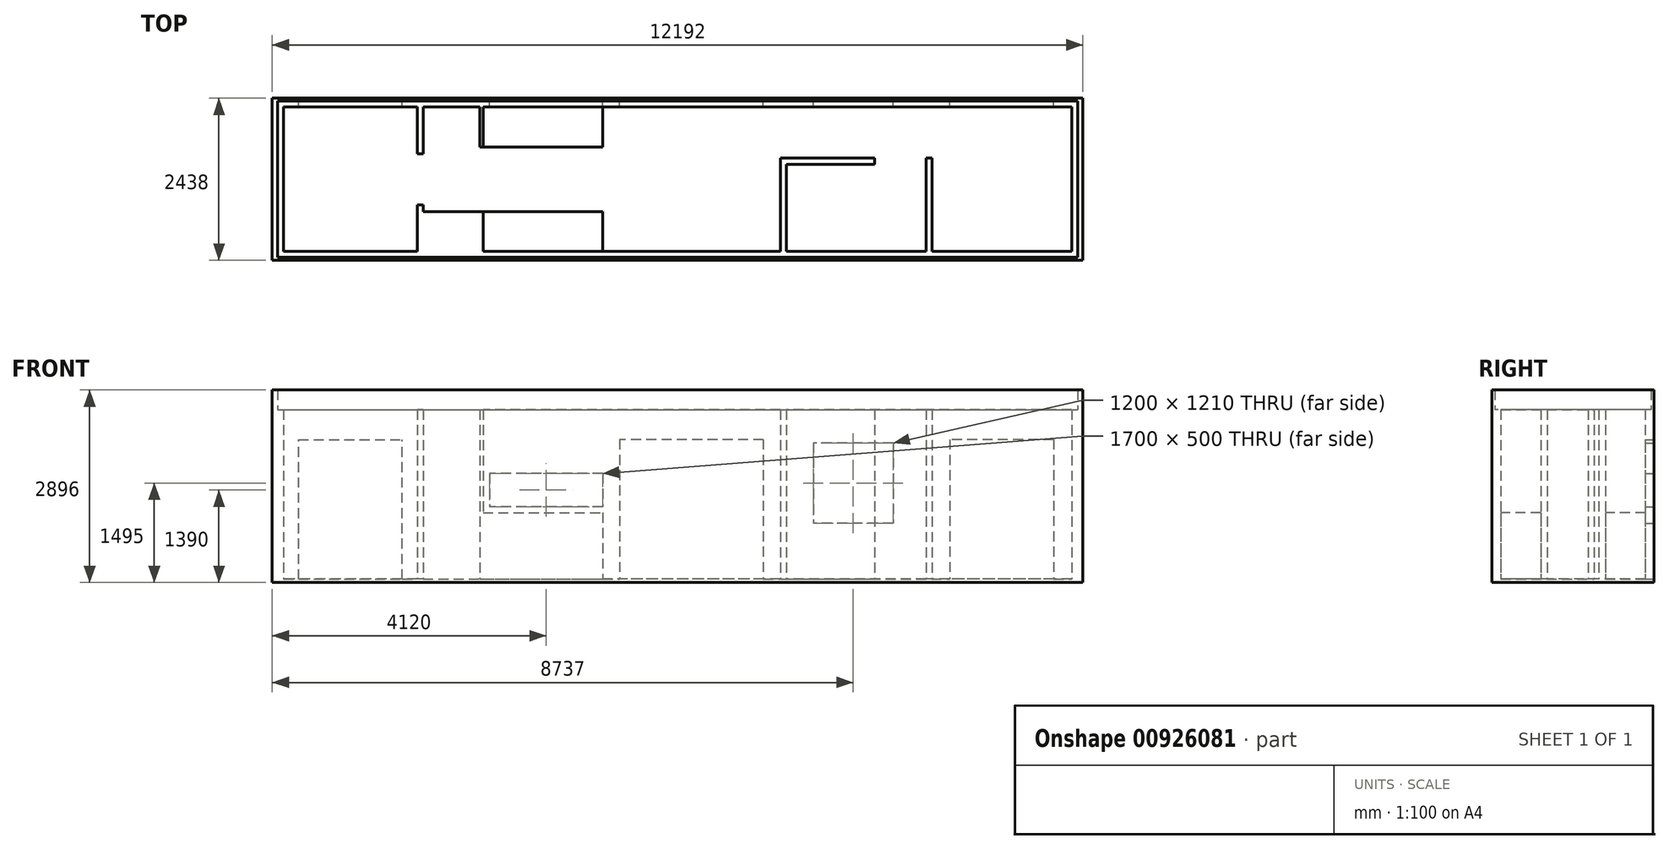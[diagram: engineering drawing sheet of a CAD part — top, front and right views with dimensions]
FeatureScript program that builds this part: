
annotation { "Feature Type Name" : "Feature", "Feature Type Description" : "" }
export const myFeature = defineFeature(function(context is Context, id is Id, definition is map)
    precondition{}
    {
        {
            var Q0;
            Q0=qCreatedBy(makeId("Top.planeOp"),FACE);
            var sketch = newSketch(context, id + "F0", { "sketchPlane" : qUnion([Q0])});
            skLineSegment(sketch, "E0.bottom", {"start": v(-6016, 1176) * mm, "end": v(6016, 1176) * mm});
            skLineSegment(sketch, "E0.top", {"start": v(-6016, -1176) * mm, "end": v(6016, -1176) * mm});
            skLineSegment(sketch, "E0.left", {"start": v(-6016, 1176) * mm, "end": v(-6016, -1176) * mm});
            skLineSegment(sketch, "E0.right", {"start": v(6016, 1176) * mm, "end": v(6016, -1176) * mm});
            skPoint(sketch, "E0.middle", {"position": v(0, 0) * mm});
            skLineSegment(sketch, "E1.bottom", {"start": v(-6096, 1219) * mm, "end": v(6096, 1219) * mm});
            skLineSegment(sketch, "E1.top", {"start": v(-6096, -1219) * mm, "end": v(6096, -1219) * mm});
            skLineSegment(sketch, "E1.left", {"start": v(-6096, 1219) * mm, "end": v(-6096, -1219) * mm});
            skLineSegment(sketch, "E1.right", {"start": v(6096, 1219) * mm, "end": v(6096, -1219) * mm});
            skSolve(sketch);
        }
        {
            var Q0;
            Q0=makeQuery(id+"F0.imprint","IMPRINT",FACE,{"disambiguationData":[TD([[makeQuery(id+"F0.imprint","IMPRINT",EDGE,{"derivedFrom":sQuery(id+"F0.wireOp",EDGE,"E0.bottom")}),1.0]])]});
            extrude(context, id + "F1", {"entities" : qUnion([Q0]), "depth" : 2896 * mm, "offsetDistance" : 25 * mm});
        }
        {
            var Q0;
            Q0=makeQuery(id+"F0.imprint","IMPRINT",FACE,{"disambiguationData":[TD([[makeQuery(id+"F0.imprint","IMPRINT",EDGE,{"derivedFrom":sQuery(id+"F0.wireOp",EDGE,"E0.bottom")}),-1.0]])]});
            extrude(context, id + "F2", {"entities" : qUnion([Q0]), "operationType" : NewBodyOperationType.ADD, "depth" : 50 * mm, "offsetDistance" : 25 * mm});
        }
        {
            var Q0;
            Q0=makeQuery(id+"F2.opExtrude","CAP_FACE",FACE,{"disambiguationData":[OSD([sQuery(id+"F0.wireOp",EDGE,"E0.bottom"),sQuery(id+"F0.wireOp",EDGE,"E0.top"),sQuery(id+"F0.wireOp",EDGE,"E0.left"),sQuery(id+"F0.wireOp",EDGE,"E0.right")])],"isStart":false});
            var sketch = newSketch(context, id + "F3", { "sketchPlane" : qUnion([Q0])});
            skLineSegment(sketch, "E2.bottom", {"start": v(-6016, 1176) * mm, "end": v(-5926, 1176) * mm});
            skLineSegment(sketch, "E2.top", {"start": v(-6016, -1176) * mm, "end": v(-5926, -1176) * mm});
            skLineSegment(sketch, "E2.left", {"start": v(-6016, 1176) * mm, "end": v(-6016, -1176) * mm});
            skLineSegment(sketch, "E2.right", {"start": v(-5926, 1086) * mm, "end": v(-5926, -1086) * mm});
            skLineSegment(sketch, "E3.bottom", {"start": v(-5926, 1176) * mm, "end": v(6016, 1176) * mm});
            skLineSegment(sketch, "E3.top", {"start": v(-5926, 1086) * mm, "end": v(5926, 1086) * mm});
            skLineSegment(sketch, "E4.top", {"start": v(5926, -1176) * mm, "end": v(6016, -1176) * mm});
            skLineSegment(sketch, "E4.left", {"start": v(5926, 1086) * mm, "end": v(5926, -1086) * mm});
            skLineSegment(sketch, "E5.bottom", {"start": v(5926, -1086) * mm, "end": v(-5926, -1086) * mm});
            skLineSegment(sketch, "E5.top", {"start": v(5926, -1176) * mm, "end": v(-5926, -1176) * mm});
            skSolve(sketch);
        }
        {
            var Q0;
            Q0=makeQuery(id+"F3.imprint","IMPRINT",FACE,{"disambiguationData":[TD([[makeQuery(id+"F3.imprint","IMPRINT",EDGE,{"derivedFrom":sQuery(id+"F3.wireOp",EDGE,"E2.bottom")}),-1.0]])]});
            extrude(context, id + "F4", {"entities" : qUnion([Q0]), "operationType" : NewBodyOperationType.ADD, "depth" : 2550 * mm, "offsetDistance" : 25 * mm});
        }
        {
            var Q0;
            Q0=makeQuery(id+"F2.opExtrude","CAP_FACE",FACE,{"disambiguationData":[OSD([sQuery(id+"F0.wireOp",EDGE,"E0.bottom"),sQuery(id+"F0.wireOp",EDGE,"E0.top"),sQuery(id+"F0.wireOp",EDGE,"E0.left"),sQuery(id+"F0.wireOp",EDGE,"E0.right")])],"isStart":false});
            var sketch = newSketch(context, id + "F5", { "sketchPlane" : qUnion([Q0])});
            skLineSegment(sketch, "E6.bottom", {"start": v(-3826, 1086) * mm, "end": v(-3916, 1086) * mm});
            skLineSegment(sketch, "E6.top", {"start": v(-3826, 385) * mm, "end": v(-3916, 385) * mm});
            skLineSegment(sketch, "E6.left", {"start": v(-3826, 1086) * mm, "end": v(-3826, 385) * mm});
            skLineSegment(sketch, "E6.right", {"start": v(-3916, 1086) * mm, "end": v(-3916, 385) * mm});
            skLineSegment(sketch, "E7.bottom", {"start": v(-3826, -385) * mm, "end": v(-3916, -385) * mm});
            skLineSegment(sketch, "E7.top", {"start": v(-3826, -1086) * mm, "end": v(-3916, -1086) * mm});
            skLineSegment(sketch, "E7.left", {"start": v(-3826, -385) * mm, "end": v(-3826, -1086) * mm});
            skLineSegment(sketch, "E7.right", {"start": v(-3916, -385) * mm, "end": v(-3916, -1086) * mm});
            skLineSegment(sketch, "E8.bottom", {"start": v(-3826, -1086) * mm, "end": v(-2926, -1086) * mm});
            skLineSegment(sketch, "E8.top", {"start": v(-3826, -486) * mm, "end": v(-2926, -486) * mm});
            skLineSegment(sketch, "E8.left", {"start": v(-3826, -1086) * mm, "end": v(-3826, -486) * mm});
            skLineSegment(sketch, "E8.right", {"start": v(-2926, -1086) * mm, "end": v(-2926, -486) * mm});
            skLineSegment(sketch, "E9.bottom", {"start": v(-2926, -486) * mm, "end": v(-1126, -486) * mm});
            skLineSegment(sketch, "E9.top", {"start": v(-2926, -1086) * mm, "end": v(-1126, -1086) * mm});
            skLineSegment(sketch, "E9.left", {"start": v(-2926, -486) * mm, "end": v(-2926, -1086) * mm});
            skLineSegment(sketch, "E9.right", {"start": v(-1126, -486) * mm, "end": v(-1126, -1086) * mm});
            skLineSegment(sketch, "E10.bottom", {"start": v(3826, -1086) * mm, "end": v(3736, -1086) * mm});
            skLineSegment(sketch, "E10.top", {"start": v(3826, 316) * mm, "end": v(3736, 316) * mm});
            skLineSegment(sketch, "E10.left", {"start": v(3826, -1086) * mm, "end": v(3826, 316) * mm});
            skLineSegment(sketch, "E10.right", {"start": v(3736, -1086) * mm, "end": v(3736, 316) * mm});
            skLineSegment(sketch, "E11.bottom", {"start": v(1546, -1086) * mm, "end": v(1636, -1086) * mm});
            skLineSegment(sketch, "E11.top", {"start": v(1546, 316) * mm, "end": v(1636, 316) * mm});
            skLineSegment(sketch, "E11.left", {"start": v(1546, -1086) * mm, "end": v(1546, 316) * mm});
            skLineSegment(sketch, "E11.right", {"start": v(1636, -1086) * mm, "end": v(1636, 226) * mm});
            skLineSegment(sketch, "E12.bottom", {"start": v(1636, 316) * mm, "end": v(2966, 316) * mm});
            skLineSegment(sketch, "E12.top", {"start": v(1636, 226) * mm, "end": v(2966, 226) * mm});
            skLineSegment(sketch, "E12.right", {"start": v(2966, 316) * mm, "end": v(2966, 226) * mm});
            skLineSegment(sketch, "E13.bottom", {"start": v(-2976, 1086) * mm, "end": v(-2926, 1086) * mm});
            skLineSegment(sketch, "E13.top", {"start": v(-2976, 486) * mm, "end": v(-2926, 486) * mm});
            skLineSegment(sketch, "E13.left", {"start": v(-2976, 1086) * mm, "end": v(-2976, 486) * mm});
            skLineSegment(sketch, "E13.right", {"start": v(-2926, 1086) * mm, "end": v(-2926, 486) * mm});
            skLineSegment(sketch, "E14.bottom", {"start": v(-2926, 486) * mm, "end": v(-1126, 486) * mm});
            skLineSegment(sketch, "E14.top", {"start": v(-2926, 1086) * mm, "end": v(-1126, 1086) * mm});
            skLineSegment(sketch, "E14.left", {"start": v(-2926, 486) * mm, "end": v(-2926, 1086) * mm});
            skLineSegment(sketch, "E14.right", {"start": v(-1126, 486) * mm, "end": v(-1126, 1086) * mm});
            skSolve(sketch);
        }
        {
            var Q0;
            Q0=makeQuery(id+"F5.imprint","IMPRINT",FACE,{"disambiguationData":[TD([[makeQuery(id+"F5.imprint","IMPRINT",EDGE,{"derivedFrom":sQuery(id+"F5.wireOp",EDGE,"E6.bottom")}),-1.0]])]});
            var Q1;
            {var subQ1=sQuery(id+"F5.wireOp",EDGE,"E7.bottom");Q1=makeQuery(id+"F5.imprint","IMPRINT",FACE,{"disambiguationData":[TD([[makeQuery(id+"F5.imprint","IMPRINT",EDGE,{"derivedFrom":subQ1}),1.0]])]});}
            var Q2;
            Q2=makeQuery(id+"F5.imprint","IMPRINT",FACE,{"disambiguationData":[TD([[makeQuery(id+"F5.imprint","IMPRINT",EDGE,{"derivedFrom":sQuery(id+"F5.wireOp",EDGE,"E11.bottom")}),-1.0]])]});
            var Q3;
            Q3=makeQuery(id+"F5.imprint","IMPRINT",FACE,{"disambiguationData":[TD([[makeQuery(id+"F5.imprint","IMPRINT",EDGE,{"derivedFrom":sQuery(id+"F5.wireOp",EDGE,"E10.bottom")}),-1.0]])]});
            var Q4;
            Q4=makeQuery(id+"F5.imprint","IMPRINT",FACE,{"disambiguationData":[TD([[makeQuery(id+"F5.imprint","IMPRINT",EDGE,{"derivedFrom":sQuery(id+"F5.wireOp",EDGE,"E13.bottom")}),-1.0]])]});
            extrude(context, id + "F6", {"entities" : qUnion([Q0, Q1, Q2, Q3, Q4]), "operationType" : NewBodyOperationType.ADD, "depth" : 2550 * mm, "offsetDistance" : 25 * mm});
        }
        {
            var Q0;
            Q0=makeQuery(id+"F5.imprint","IMPRINT",FACE,{"disambiguationData":[TD([[makeQuery(id+"F5.imprint","IMPRINT",EDGE,{"derivedFrom":sQuery(id+"F5.wireOp",EDGE,"E8.right")}),-1.0]])]});
            var Q1;
            Q1=makeQuery(id+"F5.imprint","IMPRINT",FACE,{"disambiguationData":[TD([[makeQuery(id+"F5.imprint","IMPRINT",EDGE,{"derivedFrom":sQuery(id+"F5.wireOp",EDGE,"E13.right")}),1.0]])]});
            extrude(context, id + "F7", {"entities" : qUnion([Q0, Q1]), "operationType" : NewBodyOperationType.ADD, "depth" : 1000 * mm, "offsetDistance" : 25 * mm});
        }
        {
            var Q0;
            {var subQ0=sQuery(id+"F5.wireOp",EDGE,"E8.bottom");Q0=makeQuery(id+"F5.imprint","IMPRINT",FACE,{"disambiguationData":[TD([[makeQuery(id+"F5.imprint","IMPRINT",EDGE,{"derivedFrom":subQ0}),-1.0]])]});}
            extrude(context, id + "F8", {"entities" : qUnion([Q0]), "operationType" : NewBodyOperationType.ADD, "depth" : 2550 * mm, "offsetDistance" : 25 * mm});
        }
        {
            var Q0;
            Q0=makeQuery(id+"F1.opExtrude","SWEPT_FACE",FACE,{"disambiguationData":[OSD([sQuery(id+"F0.wireOp",EDGE,"E1.bottom")])]});
            var sketch = newSketch(context, id + "F9", { "sketchPlane" : qUnion([Q0])});
            skLineSegment(sketch, "E15.bottom", {"start": v(-1290, 2150) * mm, "end": v(870, 2150) * mm});
            skLineSegment(sketch, "E15.top", {"start": v(-1290, 50) * mm, "end": v(870, 50) * mm});
            skLineSegment(sketch, "E15.left", {"start": v(-1290, 2150) * mm, "end": v(-1290, 50) * mm});
            skLineSegment(sketch, "E15.right", {"start": v(870, 2150) * mm, "end": v(870, 50) * mm});
            skLineSegment(sketch, "E16.bottom", {"start": v(1126, 1640) * mm, "end": v(2826, 1640) * mm});
            skLineSegment(sketch, "E16.top", {"start": v(1126, 1140) * mm, "end": v(2826, 1140) * mm});
            skLineSegment(sketch, "E16.left", {"start": v(1126, 1640) * mm, "end": v(1126, 1140) * mm});
            skLineSegment(sketch, "E16.right", {"start": v(2826, 1640) * mm, "end": v(2826, 1140) * mm});
            skLineSegment(sketch, "E17.bottom", {"start": v(-5656, 2150) * mm, "end": v(-4096, 2150) * mm});
            skLineSegment(sketch, "E17.top", {"start": v(-5656, 50) * mm, "end": v(-4096, 50) * mm});
            skLineSegment(sketch, "E17.left", {"start": v(-5656, 2150) * mm, "end": v(-5656, 50) * mm});
            skLineSegment(sketch, "E17.right", {"start": v(-4096, 2150) * mm, "end": v(-4096, 50) * mm});
            skLineSegment(sketch, "E18.bottom", {"start": v(5701, 50) * mm, "end": v(4141, 50) * mm});
            skLineSegment(sketch, "E18.top", {"start": v(5701, 2150) * mm, "end": v(4141, 2150) * mm});
            skLineSegment(sketch, "E18.left", {"start": v(5701, 50) * mm, "end": v(5701, 2150) * mm});
            skLineSegment(sketch, "E18.right", {"start": v(4141, 50) * mm, "end": v(4141, 2150) * mm});
            skLineSegment(sketch, "E19.bottom", {"start": v(-3241, 2100) * mm, "end": v(-2041, 2100) * mm});
            skLineSegment(sketch, "E19.top", {"start": v(-3241, 890) * mm, "end": v(-2041, 890) * mm});
            skLineSegment(sketch, "E19.left", {"start": v(-3241, 2100) * mm, "end": v(-3241, 890) * mm});
            skLineSegment(sketch, "E19.right", {"start": v(-2041, 2100) * mm, "end": v(-2041, 890) * mm});
            skSolve(sketch);
        }
        {
            var Q0;
            Q0=makeQuery(id+"F9.imprint","IMPRINT",FACE,{"disambiguationData":[TD([[makeQuery(id+"F9.imprint","IMPRINT",EDGE,{"derivedFrom":sQuery(id+"F9.wireOp",EDGE,"E15.bottom")}),-1.0]])]});
            var Q1;
            Q1=makeQuery(id+"F9.imprint","IMPRINT",FACE,{"disambiguationData":[TD([[makeQuery(id+"F9.imprint","IMPRINT",EDGE,{"derivedFrom":sQuery(id+"F9.wireOp",EDGE,"E16.bottom")}),-1.0]])]});
            var Q2;
            Q2=makeQuery(id+"F9.imprint","IMPRINT",FACE,{"disambiguationData":[TD([[makeQuery(id+"F9.imprint","IMPRINT",EDGE,{"derivedFrom":sQuery(id+"F9.wireOp",EDGE,"E17.bottom")}),-1.0]])]});
            var Q3;
            Q3=makeQuery(id+"F9.imprint","IMPRINT",FACE,{"disambiguationData":[TD([[makeQuery(id+"F9.imprint","IMPRINT",EDGE,{"derivedFrom":sQuery(id+"F9.wireOp",EDGE,"E18.bottom")}),-1.0]])]});
            var Q4;
            Q4=makeQuery(id+"F9.imprint","IMPRINT",FACE,{"disambiguationData":[TD([[makeQuery(id+"F9.imprint","IMPRINT",EDGE,{"derivedFrom":sQuery(id+"F9.wireOp",EDGE,"E19.bottom")}),-1.0]])]});
            extrude(context, id + "F10", {"entities" : qUnion([Q0, Q1, Q2, Q3, Q4]), "operationType" : NewBodyOperationType.REMOVE, "oppositeDirection" : true, "depth" : 135 * mm, "offsetDistance" : 25 * mm});
        }
    });
